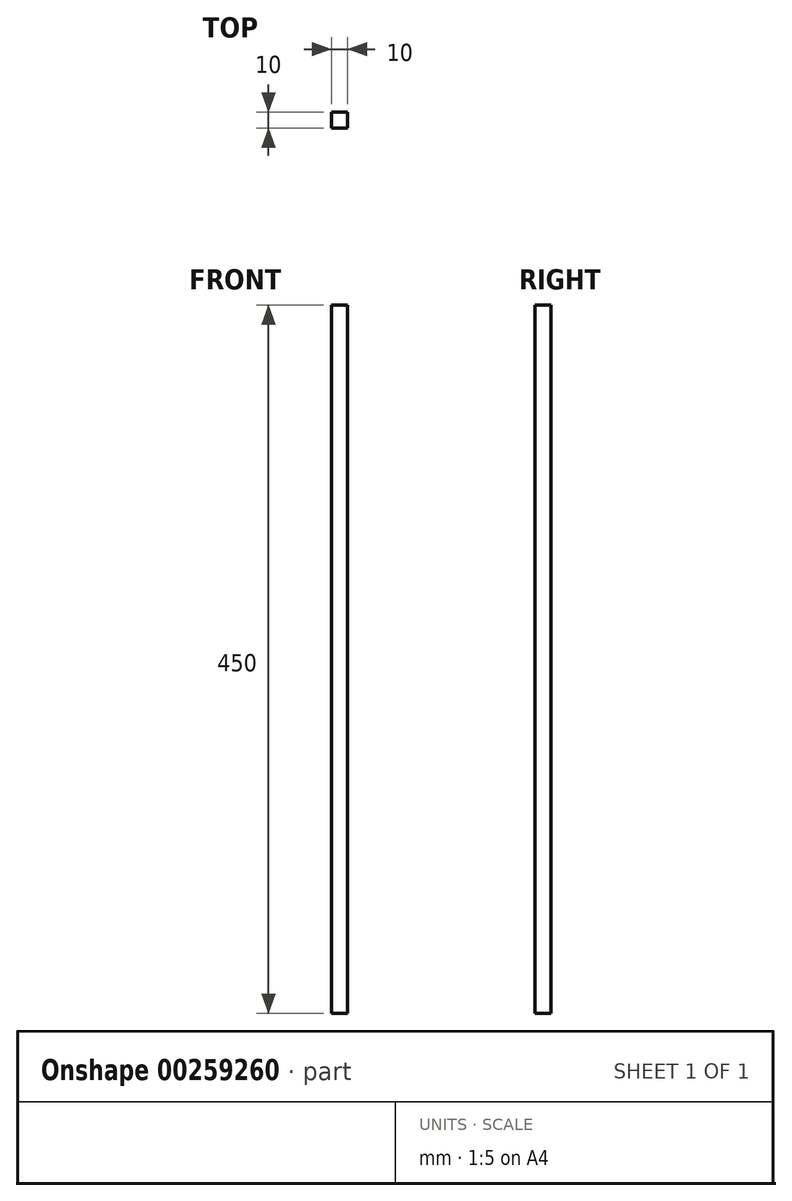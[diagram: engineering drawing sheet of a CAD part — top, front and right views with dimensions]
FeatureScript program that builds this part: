
annotation { "Feature Type Name" : "Feature", "Feature Type Description" : "" }
export const myFeature = defineFeature(function(context is Context, id is Id, definition is map)
    precondition{}
    {
        {
            var Q0;
            Q0=qCreatedBy(makeId("Top.planeOp"),FACE);
            var sketch = newSketch(context, id + "F0", { "sketchPlane" : qUnion([Q0])});
            skLineSegment(sketch, "E0.bottom", {"start": v(-4.67, 5.16) * mm, "end": v(5.33, 5.16) * mm});
            skLineSegment(sketch, "E0.top", {"start": v(-4.67, -4.84) * mm, "end": v(5.33, -4.84) * mm});
            skLineSegment(sketch, "E0.left", {"start": v(-4.67, 5.16) * mm, "end": v(-4.67, -4.84) * mm});
            skLineSegment(sketch, "E0.right", {"start": v(5.33, 5.16) * mm, "end": v(5.33, -4.84) * mm});
            skSolve(sketch);
        }
        {
            var Q0;
            Q0=makeQuery(id+"F0.imprint","IMPRINT",FACE,{"disambiguationData":[TD([[makeQuery(id+"F0.imprint","IMPRINT",EDGE,{"derivedFrom":sQuery(id+"F0.wireOp",EDGE,"E0.bottom")}),-1.0]])]});
            extrude(context, id + "F1", {"entities" : qUnion([Q0]), "depth" : 450 * mm});
        }
    });
